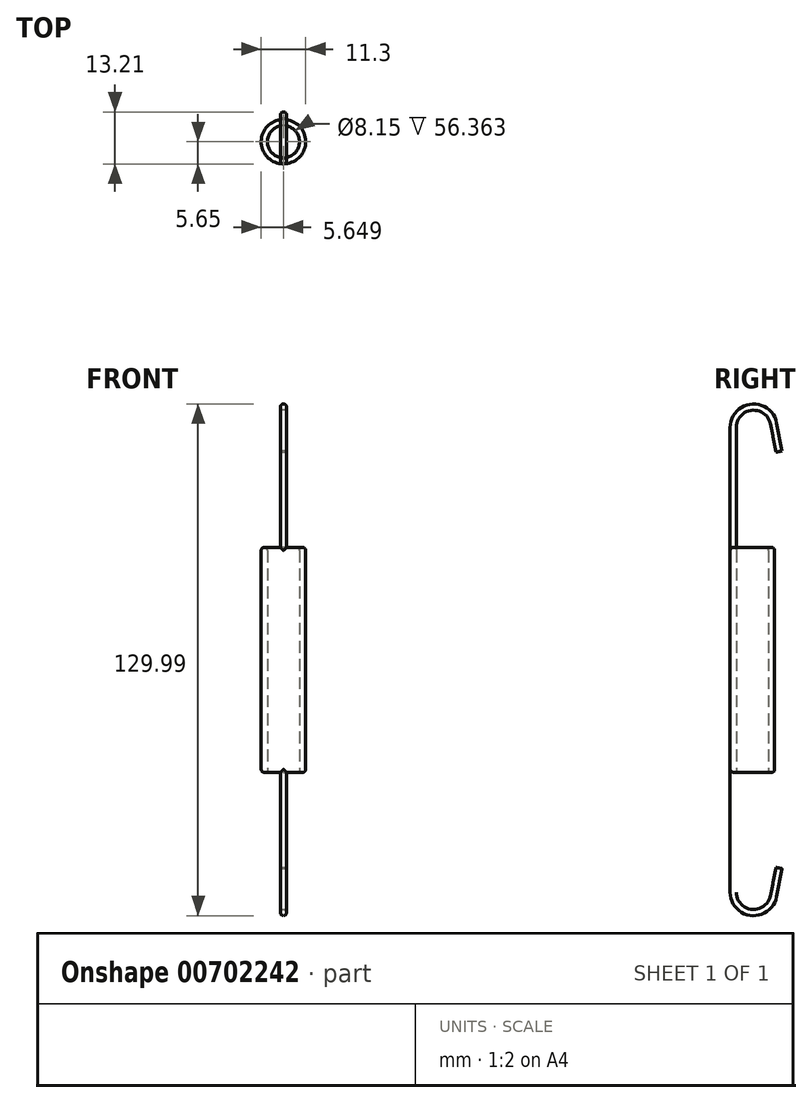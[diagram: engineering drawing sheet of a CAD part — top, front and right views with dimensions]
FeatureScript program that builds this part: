
annotation { "Feature Type Name" : "Feature", "Feature Type Description" : "" }
export const myFeature = defineFeature(function(context is Context, id is Id, definition is map)
    precondition{}
    {
        {
            var Q0;
            Q0=qCreatedBy(makeId("Top.planeOp"),FACE);
            var sketch = newSketch(context, id + "F0", { "sketchPlane" : qUnion([Q0])});
            skCircle(sketch, "E0", {"center": v(-5.65, 0) * mm, "radius": 5.65 * mm});
            skCircle(sketch, "E1", {"center": v(-5.65, 0) * mm, "radius": 4.08 * mm});
            skSolve(sketch);
        }
        {
            var Q0;
            Q0=makeQuery(id+"F0.imprint","IMPRINT",FACE,{"disambiguationData":[TD([[makeQuery(id+"F0.imprint","IMPRINT",EDGE,{"derivedFrom":sQuery(id+"F0.wireOp",EDGE,"E0")}),1.0]])]});
            extrude(context, id + "F1", {"entities" : qUnion([Q0]), "depth" : 57.15 * mm, "offsetDistance" : 25.4 * mm});
        }
        {
            var Q0;
            Q0=qCreatedBy(makeId("Right.planeOp"),FACE);
            var sketch = newSketch(context, id + "F2", { "sketchPlane" : qUnion([Q0])});
            skLineSegment(sketch, "E2.0", {"start": v(-5.65, 0) * mm, "end": v(5.65, 0) * mm});
            skLineSegment(sketch, "E3.bottom", {"start": v(-5.65, 0) * mm, "end": v(6.26, 0) * mm});
            skLineSegment(sketch, "E3.top", {"start": v(-5.65, -36.42) * mm, "end": v(6.26, -36.42) * mm});
            skLineSegment(sketch, "E3.left", {"start": v(-5.65, 0) * mm, "end": v(-5.65, -36.42) * mm});
            skLineSegment(sketch, "E3.right", {"start": v(6.26, 0) * mm, "end": v(6.26, -36.42) * mm});
            skLineSegment(sketch, "E4.0", {"start": v(-5.65, 57.15) * mm, "end": v(5.65, 57.15) * mm});
            skLineSegment(sketch, "E5.bottom", {"start": v(-5.65, 57.15) * mm, "end": v(6.26, 57.15) * mm});
            skLineSegment(sketch, "E5.top", {"start": v(-5.65, 93.57) * mm, "end": v(6.26, 93.57) * mm});
            skLineSegment(sketch, "E5.left", {"start": v(-5.65, 57.15) * mm, "end": v(-5.65, 93.57) * mm});
            skLineSegment(sketch, "E5.right", {"start": v(6.26, 57.15) * mm, "end": v(6.26, 93.57) * mm});
            skArc(sketch, "E6", {"start": v(-5.65, -30.47) * mm, "mid": v(-0.27, -36.4) * mm, "end": v(6.15, -31.62) * mm});
            skPoint(sketch, "E6.centerSnap0", {"position": v(0.3, -36.42) * mm});
            skArc(sketch, "E7", {"start": v(6.15, 88.77) * mm, "mid": v(-0.27, 93.55) * mm, "end": v(-5.65, 87.62) * mm});
            skPoint(sketch, "E7.centerSnap0", {"position": v(0.3, 93.57) * mm});
            skLineSegment(sketch, "E8", {"start": v(1.87, 81.64) * mm, "end": v(14.82, 81.64) * mm});
            skLineSegment(sketch, "E9", {"start": v(7.56, 80.48) * mm, "end": v(7.56, 83.95) * mm});
            skLineSegment(sketch, "E10", {"start": v(8.6, -24.49) * mm, "end": v(15.97, -24.49) * mm});
            skLineSegment(sketch, "E11", {"start": v(7.56, -26.21) * mm, "end": v(7.56, -20.09) * mm});
            skLineSegment(sketch, "E12", {"start": v(7.56, -24.49) * mm, "end": v(6.15, -31.62) * mm});
            skLineSegment(sketch, "E13", {"start": v(7.56, 81.64) * mm, "end": v(6.15, 88.77) * mm});
            skLineSegment(sketch, "E14.0", {"start": v(-4.08, 0) * mm, "end": v(-4.08, -30.47) * mm});
            skCircle(sketch, "E15", {"center": v(0.3, -30.47) * mm, "radius": 4.38 * mm});
            skLineSegment(sketch, "E16.0", {"start": v(6.01, -24.18) * mm, "end": v(4.6, -31.32) * mm});
            skLineSegment(sketch, "E17", {"start": v(7.56, -24.49) * mm, "end": v(6.01, -24.18) * mm});
            skLineSegment(sketch, "E18.0", {"start": v(-4.08, 57.15) * mm, "end": v(-4.08, 87.62) * mm});
            skLineSegment(sketch, "E19.0", {"start": v(6.01, 81.33) * mm, "end": v(4.6, 88.47) * mm});
            skCircle(sketch, "E20", {"center": v(0.3, 87.62) * mm, "radius": 4.38 * mm});
            skLineSegment(sketch, "E21.trimOffspring", {"start": v(-4.08, 91.65) * mm, "end": v(-4.08, 93.57) * mm});
            skLineSegment(sketch, "E22.trimOffspring", {"start": v(-4.08, -34.5) * mm, "end": v(-4.08, -36.42) * mm});
            skLineSegment(sketch, "E23", {"start": v(7.56, 81.64) * mm, "end": v(6.01, 81.33) * mm});
            skSolve(sketch);
        }
        {
            var Q0;
            {var subQ0=sQuery(id+"F2.wireOp",EDGE,"E18.0");Q0=makeQuery(id+"F2.imprint","IMPRINT",FACE,{"disambiguationData":[TD([[makeQuery(id+"F2.imprint","IMPRINT",EDGE,{"derivedFrom":subQ0}),1.0]])]});}
            var Q1;
            {var subQ0=sQuery(id+"F2.wireOp",EDGE,"E13");var subQ1=sQuery(id+"F2.wireOp",EDGE,"E5.right");var subQ2=makeQuery(id+"F2.imprint","INTERSECT",VERTEX,{"derivedFrom":[subQ1,subQ0]});Q1=makeQuery(id+"F2.imprint","IMPRINT",FACE,{"disambiguationData":[TD([[makeQuery(id+"F2.imprint","IMPRINT",EDGE,{"disambiguationData":[TD([[subQ2,1.0]])],"derivedFrom":subQ1}),-1.0]])]});}
            var Q2;
            {var subQ0=sQuery(id+"F2.wireOp",EDGE,"E23");var subQ1=sQuery(id+"F2.wireOp",EDGE,"E5.right");var subQ2=makeQuery(id+"F2.imprint","INTERSECT",VERTEX,{"derivedFrom":[subQ1,subQ0]});Q2=makeQuery(id+"F2.imprint","IMPRINT",FACE,{"disambiguationData":[TD([[makeQuery(id+"F2.imprint","IMPRINT",EDGE,{"disambiguationData":[TD([[subQ2,-1.0]])],"derivedFrom":subQ1}),-1.0]])]});}
            var Q3;
            {var subQ0=sQuery(id+"F2.wireOp",EDGE,"E23");var subQ1=sQuery(id+"F2.wireOp",EDGE,"E5.right");var subQ2=makeQuery(id+"F2.imprint","INTERSECT",VERTEX,{"derivedFrom":[subQ1,subQ0]});Q3=makeQuery(id+"F2.imprint","IMPRINT",FACE,{"disambiguationData":[TD([[makeQuery(id+"F2.imprint","IMPRINT",EDGE,{"disambiguationData":[TD([[subQ2,-1.0]])],"derivedFrom":subQ1}),1.0]])]});}
            var Q4;
            {var subQ9=sQuery(id+"F2.wireOp",EDGE,"E14.0");Q4=makeQuery(id+"F2.imprint","IMPRINT",FACE,{"disambiguationData":[TD([[makeQuery(id+"F2.imprint","IMPRINT",EDGE,{"derivedFrom":subQ9}),-1.0]])]});}
            var Q5;
            {var subQ0=sQuery(id+"F2.wireOp",EDGE,"E17");var subQ1=sQuery(id+"F2.wireOp",EDGE,"E3.right");var subQ2=makeQuery(id+"F2.imprint","INTERSECT",VERTEX,{"derivedFrom":[subQ1,subQ0]});Q5=makeQuery(id+"F2.imprint","IMPRINT",FACE,{"disambiguationData":[TD([[makeQuery(id+"F2.imprint","IMPRINT",EDGE,{"disambiguationData":[TD([[subQ2,-1.0]])],"derivedFrom":subQ1}),1.0]])]});}
            extrude(context, id + "F3", {"entities" : qUnion([Q0, Q1, Q2, Q3, Q4, Q5]), "operationType" : NewBodyOperationType.ADD, "oppositeDirection" : true, "depth" : 11.3 * mm, "offsetDistance" : 25.4 * mm});
        }
        {
            var Q0;
            Q0=makeQuery(id+"F1.opExtrude","CAP_FACE",FACE,{"disambiguationData":[OSD([sQuery(id+"F0.wireOp",EDGE,"E0"),sQuery(id+"F0.wireOp",EDGE,"E1")])],"isStart":false});
            var sketch = newSketch(context, id + "F4", { "sketchPlane" : qUnion([Q0])});
            skLineSegment(sketch, "E24", {"start": v(-5.65, 0) * mm, "end": v(-5.65, -4.08) * mm});
            skLineSegment(sketch, "E25", {"start": v(-5.65, -4.08) * mm, "end": v(-6.44, -4.08) * mm});
            skLineSegment(sketch, "E26", {"start": v(-6.44, -4.08) * mm, "end": v(-4.86, -4.08) * mm});
            skLineSegment(sketch, "E27.bottom", {"start": v(-6.44, -4.08) * mm, "end": v(-11.86, -4.08) * mm});
            skLineSegment(sketch, "E27.top", {"start": v(-6.44, -7.3) * mm, "end": v(-11.86, -7.3) * mm});
            skLineSegment(sketch, "E27.left", {"start": v(-6.44, -4.08) * mm, "end": v(-6.44, -7.3) * mm});
            skLineSegment(sketch, "E27.right", {"start": v(-11.86, -4.08) * mm, "end": v(-11.86, -7.3) * mm});
            skLineSegment(sketch, "E28.bottom", {"start": v(-4.86, -4.08) * mm, "end": v(1.36, -4.08) * mm});
            skLineSegment(sketch, "E28.top", {"start": v(-4.86, -7.3) * mm, "end": v(1.36, -7.3) * mm});
            skLineSegment(sketch, "E28.left", {"start": v(-4.86, -4.08) * mm, "end": v(-4.86, -7.3) * mm});
            skLineSegment(sketch, "E28.right", {"start": v(1.36, -4.08) * mm, "end": v(1.36, -7.3) * mm});
            skLineSegment(sketch, "E29.bottom", {"start": v(-11.86, -4.08) * mm, "end": v(-6.44, -4.08) * mm});
            skLineSegment(sketch, "E29.top", {"start": v(-11.86, 8.59) * mm, "end": v(-6.44, 8.59) * mm});
            skLineSegment(sketch, "E29.left", {"start": v(-11.86, -4.08) * mm, "end": v(-11.86, 8.59) * mm});
            skLineSegment(sketch, "E29.right", {"start": v(-6.44, -4.08) * mm, "end": v(-6.44, 8.59) * mm});
            skLineSegment(sketch, "E30.top", {"start": v(-4.86, 8.63) * mm, "end": v(1.36, 8.63) * mm});
            skLineSegment(sketch, "E30.left", {"start": v(-4.86, -4.08) * mm, "end": v(-4.86, 8.63) * mm});
            skLineSegment(sketch, "E30.right", {"start": v(1.36, -4.08) * mm, "end": v(1.36, 8.63) * mm});
            skSolve(sketch);
        }
        {
            var Q0;
            {var subQ2=sQuery(id+"F4.wireOp",EDGE,"E29.top");Q0=makeQuery(id+"F4.imprint","IMPRINT",FACE,{"disambiguationData":[TD([[makeQuery(id+"F4.imprint","IMPRINT",EDGE,{"derivedFrom":subQ2}),-1.0]])]});}
            var Q1;
            {var subQ2=sQuery(id+"F0.wireOp",EDGE,"E1");var subQ5=sQuery(id+"F4.wireOp",EDGE,"E29.right");var subQ7=makeQuery(id+"F1.opExtrude","CAP_EDGE",EDGE,{"disambiguationData":[OSD([subQ2])],"isStart":false});var subQ10=makeQuery(id+"F4.imprint","INTERSECT",VERTEX,{"disambiguationData":[OD(0.0)],"derivedFrom":[subQ7,subQ5]});Q1=makeQuery(id+"F4.imprint","IMPRINT",FACE,{"disambiguationData":[TD([[makeQuery(id+"F4.imprint","IMPRINT",EDGE,{"disambiguationData":[TD([[subQ10,1.0]])],"derivedFrom":subQ7}),-1.0]])]});}
            var Q2;
            {var subQ0=sQuery(id+"F4.wireOp",EDGE,"E29.right");var subQ1=makeQuery(id+"F1.opExtrude","CAP_EDGE",EDGE,{"disambiguationData":[OSD([sQuery(id+"F0.wireOp",EDGE,"E1")])],"isStart":false});var subQ2=makeQuery(id+"F4.imprint","INTERSECT",VERTEX,{"disambiguationData":[OD(0.0)],"derivedFrom":[subQ1,subQ0]});Q2=makeQuery(id+"F4.imprint","IMPRINT",FACE,{"disambiguationData":[TD([[makeQuery(id+"F4.imprint","IMPRINT",EDGE,{"disambiguationData":[TD([[subQ2,-1.0]])],"derivedFrom":subQ0}),1.0]])]});}
            var Q3;
            Q3=makeQuery(id+"F4.imprint","IMPRINT",FACE,{"disambiguationData":[TD([[makeQuery(id+"F4.imprint","IMPRINT",EDGE,{"derivedFrom":sQuery(id+"F4.wireOp",EDGE,"E27.top")}),-1.0]])]});
            var Q4;
            {var subQ1=sQuery(id+"F4.wireOp",EDGE,"E30.top");Q4=makeQuery(id+"F4.imprint","IMPRINT",FACE,{"disambiguationData":[TD([[makeQuery(id+"F4.imprint","IMPRINT",EDGE,{"derivedFrom":subQ1}),-1.0]])]});}
            var Q5;
            {var subQ0=sQuery(id+"F4.wireOp",EDGE,"E30.left");var subQ2=sQuery(id+"F0.wireOp",EDGE,"E1");var subQ5=makeQuery(id+"F1.opExtrude","CAP_EDGE",EDGE,{"disambiguationData":[OSD([subQ2])],"isStart":false});var subQ10=makeQuery(id+"F4.imprint","INTERSECT",VERTEX,{"disambiguationData":[OD(0.0)],"derivedFrom":[subQ5,subQ0]});Q5=makeQuery(id+"F4.imprint","IMPRINT",FACE,{"disambiguationData":[TD([[makeQuery(id+"F4.imprint","IMPRINT",EDGE,{"disambiguationData":[TD([[subQ10,-1.0]])],"derivedFrom":subQ5}),-1.0]])]});}
            var Q6;
            {var subQ0=sQuery(id+"F4.wireOp",EDGE,"E30.left");var subQ1=makeQuery(id+"F1.opExtrude","CAP_EDGE",EDGE,{"disambiguationData":[OSD([sQuery(id+"F0.wireOp",EDGE,"E1")])],"isStart":false});var subQ2=makeQuery(id+"F4.imprint","INTERSECT",VERTEX,{"disambiguationData":[OD(0.0)],"derivedFrom":[subQ1,subQ0]});Q6=makeQuery(id+"F4.imprint","IMPRINT",FACE,{"disambiguationData":[TD([[makeQuery(id+"F4.imprint","IMPRINT",EDGE,{"disambiguationData":[TD([[subQ2,-1.0]])],"derivedFrom":subQ0}),-1.0]])]});}
            var Q7;
            Q7=makeQuery(id+"F4.imprint","IMPRINT",FACE,{"disambiguationData":[TD([[makeQuery(id+"F4.imprint","IMPRINT",EDGE,{"derivedFrom":sQuery(id+"F4.wireOp",EDGE,"E28.top")}),1.0]])]});
            extrude(context, id + "F5", {"entities" : qUnion([Q0, Q1, Q2, Q3, Q4, Q5, Q6, Q7]), "operationType" : NewBodyOperationType.REMOVE, "depth" : 76.2 * mm, "offsetDistance" : 25.4 * mm});
        }
        {
            var Q0;
            Q0=makeQuery(id+"F1.opExtrude","CAP_FACE",FACE,{"disambiguationData":[OSD([sQuery(id+"F0.wireOp",EDGE,"E0"),sQuery(id+"F0.wireOp",EDGE,"E1")])],"isStart":true});
            var sketch = newSketch(context, id + "F6", { "sketchPlane" : qUnion([Q0])});
            skLineSegment(sketch, "E31", {"start": v(-5.65, 0) * mm, "end": v(-5.65, 4.08) * mm});
            skLineSegment(sketch, "E32", {"start": v(-5.65, 4.08) * mm, "end": v(-6.44, 4.08) * mm});
            skLineSegment(sketch, "E33", {"start": v(-6.44, 4.08) * mm, "end": v(-4.86, 4.08) * mm});
            skLineSegment(sketch, "E34.bottom", {"start": v(-6.44, 4.08) * mm, "end": v(-12.15, 4.08) * mm});
            skLineSegment(sketch, "E34.top", {"start": v(-6.44, 8.66) * mm, "end": v(-12.15, 8.66) * mm});
            skLineSegment(sketch, "E34.left", {"start": v(-6.44, 4.08) * mm, "end": v(-6.44, 8.66) * mm});
            skLineSegment(sketch, "E34.right", {"start": v(-12.15, 4.08) * mm, "end": v(-12.15, 8.66) * mm});
            skLineSegment(sketch, "E35.bottom", {"start": v(-4.86, 4.08) * mm, "end": v(3.43, 4.08) * mm});
            skLineSegment(sketch, "E35.top", {"start": v(-4.86, 8.66) * mm, "end": v(3.43, 8.66) * mm});
            skLineSegment(sketch, "E35.left", {"start": v(-4.86, 4.08) * mm, "end": v(-4.86, 8.66) * mm});
            skLineSegment(sketch, "E35.right", {"start": v(3.43, 4.08) * mm, "end": v(3.43, 8.66) * mm});
            skLineSegment(sketch, "E36.bottom", {"start": v(-12.15, 4.08) * mm, "end": v(-6.44, 4.08) * mm});
            skLineSegment(sketch, "E36.top", {"start": v(-12.15, -7.97) * mm, "end": v(-6.44, -7.97) * mm});
            skLineSegment(sketch, "E36.left", {"start": v(-12.15, 4.08) * mm, "end": v(-12.15, -7.97) * mm});
            skLineSegment(sketch, "E36.right", {"start": v(-6.44, 4.08) * mm, "end": v(-6.44, -7.97) * mm});
            skLineSegment(sketch, "E37.top", {"start": v(-4.86, -7.97) * mm, "end": v(3.43, -7.97) * mm});
            skLineSegment(sketch, "E37.left", {"start": v(-4.86, 4.08) * mm, "end": v(-4.86, -7.97) * mm});
            skLineSegment(sketch, "E37.right", {"start": v(3.43, 4.08) * mm, "end": v(3.43, -7.97) * mm});
            skSolve(sketch);
        }
        {
            var Q0;
            {var subQ1=sQuery(id+"F6.wireOp",EDGE,"E37.top");Q0=makeQuery(id+"F6.imprint","IMPRINT",FACE,{"disambiguationData":[TD([[makeQuery(id+"F6.imprint","IMPRINT",EDGE,{"derivedFrom":subQ1}),1.0]])]});}
            var Q1;
            Q1=makeQuery(id+"F6.imprint","IMPRINT",FACE,{"disambiguationData":[TD([[makeQuery(id+"F6.imprint","IMPRINT",EDGE,{"derivedFrom":sQuery(id+"F6.wireOp",EDGE,"E35.top")}),-1.0]])]});
            var Q2;
            {var subQ0=sQuery(id+"F6.wireOp",EDGE,"E37.left");var subQ2=sQuery(id+"F0.wireOp",EDGE,"E1");var subQ5=makeQuery(id+"F1.opExtrude","CAP_EDGE",EDGE,{"disambiguationData":[OSD([subQ2])],"isStart":true});var subQ10=makeQuery(id+"F6.imprint","INTERSECT",VERTEX,{"disambiguationData":[OD(0.0)],"derivedFrom":[subQ5,subQ0]});Q2=makeQuery(id+"F6.imprint","IMPRINT",FACE,{"disambiguationData":[TD([[makeQuery(id+"F6.imprint","IMPRINT",EDGE,{"disambiguationData":[TD([[subQ10,-1.0]])],"derivedFrom":subQ5}),1.0]])]});}
            var Q3;
            {var subQ0=sQuery(id+"F6.wireOp",EDGE,"E37.left");var subQ1=makeQuery(id+"F1.opExtrude","CAP_EDGE",EDGE,{"disambiguationData":[OSD([sQuery(id+"F0.wireOp",EDGE,"E1")])],"isStart":true});var subQ2=makeQuery(id+"F6.imprint","INTERSECT",VERTEX,{"disambiguationData":[OD(0.0)],"derivedFrom":[subQ1,subQ0]});Q3=makeQuery(id+"F6.imprint","IMPRINT",FACE,{"disambiguationData":[TD([[makeQuery(id+"F6.imprint","IMPRINT",EDGE,{"disambiguationData":[TD([[subQ2,-1.0]])],"derivedFrom":subQ0}),1.0]])]});}
            var Q4;
            {var subQ2=sQuery(id+"F6.wireOp",EDGE,"E36.top");Q4=makeQuery(id+"F6.imprint","IMPRINT",FACE,{"disambiguationData":[TD([[makeQuery(id+"F6.imprint","IMPRINT",EDGE,{"derivedFrom":subQ2}),1.0]])]});}
            var Q5;
            {var subQ2=sQuery(id+"F0.wireOp",EDGE,"E1");var subQ5=sQuery(id+"F6.wireOp",EDGE,"E36.right");var subQ7=makeQuery(id+"F1.opExtrude","CAP_EDGE",EDGE,{"disambiguationData":[OSD([subQ2])],"isStart":true});var subQ10=makeQuery(id+"F6.imprint","INTERSECT",VERTEX,{"disambiguationData":[OD(0.0)],"derivedFrom":[subQ7,subQ5]});Q5=makeQuery(id+"F6.imprint","IMPRINT",FACE,{"disambiguationData":[TD([[makeQuery(id+"F6.imprint","IMPRINT",EDGE,{"disambiguationData":[TD([[subQ10,1.0]])],"derivedFrom":subQ7}),1.0]])]});}
            var Q6;
            {var subQ0=sQuery(id+"F6.wireOp",EDGE,"E36.right");var subQ1=makeQuery(id+"F1.opExtrude","CAP_EDGE",EDGE,{"disambiguationData":[OSD([sQuery(id+"F0.wireOp",EDGE,"E1")])],"isStart":true});var subQ2=makeQuery(id+"F6.imprint","INTERSECT",VERTEX,{"disambiguationData":[OD(0.0)],"derivedFrom":[subQ1,subQ0]});Q6=makeQuery(id+"F6.imprint","IMPRINT",FACE,{"disambiguationData":[TD([[makeQuery(id+"F6.imprint","IMPRINT",EDGE,{"disambiguationData":[TD([[subQ2,-1.0]])],"derivedFrom":subQ0}),-1.0]])]});}
            var Q7;
            Q7=makeQuery(id+"F6.imprint","IMPRINT",FACE,{"disambiguationData":[TD([[makeQuery(id+"F6.imprint","IMPRINT",EDGE,{"derivedFrom":sQuery(id+"F6.wireOp",EDGE,"E34.top")}),1.0]])]});
            extrude(context, id + "F7", {"entities" : qUnion([Q0, Q1, Q2, Q3, Q4, Q5, Q6, Q7]), "operationType" : NewBodyOperationType.REMOVE, "depth" : 76.2 * mm, "offsetDistance" : 25.4 * mm});
        }
        {
            var Q0;
            Q0=makeQuery(id+"F7.boolean.opBoolean","INTERSECT",EDGE,{"derivedFrom":[makeQuery(id+"F3.opExtrude","SWEPT_FACE",FACE,{"disambiguationData":[OSD([sQuery(id+"F2.wireOp",EDGE,"E3.left")])]}),makeQuery(id+"F7.opExtrude","SWEPT_FACE",FACE,{"disambiguationData":[OSD([sQuery(id+"F6.wireOp",EDGE,"E35.left"),sQuery(id+"F6.wireOp",EDGE,"E37.left")])]})]});
            var Q1;
            Q1=makeQuery(id+"F7.boolean.opBoolean","INTERSECT",EDGE,{"derivedFrom":[makeQuery(id+"F3.opExtrude","SWEPT_FACE",FACE,{"disambiguationData":[OSD([sQuery(id+"F2.wireOp",EDGE,"E3.left")])]}),makeQuery(id+"F7.opExtrude","SWEPT_FACE",FACE,{"disambiguationData":[OSD([sQuery(id+"F6.wireOp",EDGE,"E34.left"),sQuery(id+"F6.wireOp",EDGE,"E36.right")])]})]});
            var Q2;
            Q2=makeQuery(id+"F7.boolean.opBoolean","INTERSECT",EDGE,{"derivedFrom":[makeQuery(id+"F3.opExtrude","SWEPT_FACE",FACE,{"disambiguationData":[OSD([sQuery(id+"F2.wireOp",EDGE,"E14.0")])]}),makeQuery(id+"F7.opExtrude","SWEPT_FACE",FACE,{"disambiguationData":[OSD([sQuery(id+"F6.wireOp",EDGE,"E35.left"),sQuery(id+"F6.wireOp",EDGE,"E37.left")])]})]});
            var Q3;
            Q3=makeQuery(id+"F7.boolean.opBoolean","INTERSECT",EDGE,{"derivedFrom":[makeQuery(id+"F3.opExtrude","SWEPT_FACE",FACE,{"disambiguationData":[OSD([sQuery(id+"F2.wireOp",EDGE,"E14.0")])]}),makeQuery(id+"F7.opExtrude","SWEPT_FACE",FACE,{"disambiguationData":[OSD([sQuery(id+"F6.wireOp",EDGE,"E34.left"),sQuery(id+"F6.wireOp",EDGE,"E36.right")])]})]});
            var Q4;
            Q4=makeQuery(id+"F5.boolean.opBoolean","INTERSECT",EDGE,{"derivedFrom":[makeQuery(id+"F3.opExtrude","SWEPT_FACE",FACE,{"disambiguationData":[OSD([sQuery(id+"F2.wireOp",EDGE,"E18.0")])]}),makeQuery(id+"F5.opExtrude","SWEPT_FACE",FACE,{"disambiguationData":[OSD([sQuery(id+"F4.wireOp",EDGE,"E27.left"),sQuery(id+"F4.wireOp",EDGE,"E29.right")])]})]});
            var Q5;
            Q5=makeQuery(id+"F5.boolean.opBoolean","INTERSECT",EDGE,{"derivedFrom":[makeQuery(id+"F3.opExtrude","SWEPT_FACE",FACE,{"disambiguationData":[OSD([sQuery(id+"F2.wireOp",EDGE,"E5.left")])]}),makeQuery(id+"F5.opExtrude","SWEPT_FACE",FACE,{"disambiguationData":[OSD([sQuery(id+"F4.wireOp",EDGE,"E27.left"),sQuery(id+"F4.wireOp",EDGE,"E29.right")])]})]});
            var Q6;
            Q6=makeQuery(id+"F5.boolean.opBoolean","INTERSECT",EDGE,{"derivedFrom":[makeQuery(id+"F3.opExtrude","SWEPT_FACE",FACE,{"disambiguationData":[OSD([sQuery(id+"F2.wireOp",EDGE,"E5.left")])]}),makeQuery(id+"F5.opExtrude","SWEPT_FACE",FACE,{"disambiguationData":[OSD([sQuery(id+"F4.wireOp",EDGE,"E28.left"),sQuery(id+"F4.wireOp",EDGE,"E30.left")])]})]});
            var Q7;
            Q7=makeQuery(id+"F5.boolean.opBoolean","INTERSECT",EDGE,{"derivedFrom":[makeQuery(id+"F3.opExtrude","SWEPT_FACE",FACE,{"disambiguationData":[OSD([sQuery(id+"F2.wireOp",EDGE,"E18.0")])]}),makeQuery(id+"F5.opExtrude","SWEPT_FACE",FACE,{"disambiguationData":[OSD([sQuery(id+"F4.wireOp",EDGE,"E28.left"),sQuery(id+"F4.wireOp",EDGE,"E30.left")])]})]});
            fillet(context, id + "F8", {"entities" : qUnion([Q0, Q1, Q2, Q3, Q4, Q5, Q6, Q7]), "radius" : 0.79 * mm, "tangentPropagation" : true, "allowEdgeOverflow" : false});
        }
        {
            var Q0;
            {var subQ0=sQuery(id+"F0.wireOp",EDGE,"E0");var subQ1=makeQuery(id+"F1.opExtrude","SWEPT_FACE",FACE,{"disambiguationData":[OSD([subQ0])]});var subQ2=makeQuery(id+"F3.opExtrude","SWEPT_FACE",FACE,{"disambiguationData":[OSD([sQuery(id+"F2.wireOp",EDGE,"E5.bottom")])]});var subQ3=makeQuery(id+"F1.opExtrude","CAP_EDGE",EDGE,{"disambiguationData":[OSD([subQ0])],"isStart":false});var subQ4=makeQuery(id+"F3.boolean.opBoolean","SPLIT",EDGE,{"disambiguationData":[topologyDisambiguationEdgeConnected([subQ1,subQ2]),OD(1.0)],"derivedFrom":subQ3});var subQ5=makeQuery(id+"F3.boolean.opBoolean","SPLIT",EDGE,{"disambiguationData":[topologyDisambiguationEdgeConnected([subQ1,subQ2]),OD(0.0)],"derivedFrom":subQ3});Q0=makeQuery(id+"F8.opFillet","MERGE",EDGE,{"derivedFrom":[makeQuery(id+"F5.boolean.opBoolean","MERGE",EDGE,{"derivedFrom":[makeQuery(id+"F3.boolean.opBoolean","SPLIT",EDGE,{"disambiguationData":[topologyDisambiguationEdgeConnected([subQ1,makeQuery(id+"F1.opExtrude","CAP_FACE",FACE,{"disambiguationData":[OSD([subQ0,sQuery(id+"F0.wireOp",EDGE,"E1")])],"isStart":false})])],"derivedFrom":subQ3}),subQ5,subQ4]}),makeQuery(id+"F5.boolean.opBoolean","SPLIT",EDGE,{"derivedFrom":subQ5}),makeQuery(id+"F5.boolean.opBoolean","SPLIT",EDGE,{"derivedFrom":subQ4})]});}
            var Q1;
            Q1=makeQuery(id+"F5.boolean.opBoolean","INTERSECT",EDGE,{"derivedFrom":[makeQuery(id+"F5.opExtrude","CAP_FACE",FACE,{"disambiguationData":[OSD([sQuery(id+"F4.wireOp",EDGE,"E27.top"),sQuery(id+"F4.wireOp",EDGE,"E27.left"),sQuery(id+"F4.wireOp",EDGE,"E27.right"),sQuery(id+"F4.wireOp",EDGE,"E29.top"),sQuery(id+"F4.wireOp",EDGE,"E29.left"),sQuery(id+"F4.wireOp",EDGE,"E29.right")])],"isStart":true}),makeQuery(id+"F5.opExtrude","CAP_FACE",FACE,{"disambiguationData":[OSD([sQuery(id+"F4.wireOp",EDGE,"E28.top"),sQuery(id+"F4.wireOp",EDGE,"E28.left"),sQuery(id+"F4.wireOp",EDGE,"E28.right"),sQuery(id+"F4.wireOp",EDGE,"E30.top"),sQuery(id+"F4.wireOp",EDGE,"E30.left"),sQuery(id+"F4.wireOp",EDGE,"E30.right")])],"isStart":true})]});
            fillet(context, id + "F9", {"entities" : qUnion([Q0, Q1]), "radius" : 0.79 * mm, "tangentPropagation" : true, "allowEdgeOverflow" : false});
        }
        {
            var Q0;
            {var subQ0=sQuery(id+"F0.wireOp",EDGE,"E0");var subQ1=makeQuery(id+"F1.opExtrude","SWEPT_FACE",FACE,{"disambiguationData":[OSD([subQ0])]});var subQ2=makeQuery(id+"F3.opExtrude","SWEPT_FACE",FACE,{"disambiguationData":[OSD([sQuery(id+"F2.wireOp",EDGE,"E3.bottom")])]});var subQ3=makeQuery(id+"F1.opExtrude","CAP_EDGE",EDGE,{"disambiguationData":[OSD([subQ0])],"isStart":true});var subQ4=makeQuery(id+"F3.boolean.opBoolean","SPLIT",EDGE,{"disambiguationData":[topologyDisambiguationEdgeConnected([subQ1,subQ2]),OD(1.0)],"derivedFrom":subQ3});var subQ5=makeQuery(id+"F3.boolean.opBoolean","SPLIT",EDGE,{"disambiguationData":[topologyDisambiguationEdgeConnected([subQ1,subQ2]),OD(0.0)],"derivedFrom":subQ3});Q0=makeQuery(id+"F8.opFillet","MERGE",EDGE,{"derivedFrom":[makeQuery(id+"F7.boolean.opBoolean","MERGE",EDGE,{"derivedFrom":[makeQuery(id+"F3.boolean.opBoolean","SPLIT",EDGE,{"disambiguationData":[topologyDisambiguationEdgeConnected([subQ1,makeQuery(id+"F1.opExtrude","CAP_FACE",FACE,{"disambiguationData":[OSD([subQ0,sQuery(id+"F0.wireOp",EDGE,"E1")])],"isStart":true})])],"derivedFrom":subQ3}),subQ5,subQ4]}),makeQuery(id+"F7.boolean.opBoolean","SPLIT",EDGE,{"derivedFrom":subQ5}),makeQuery(id+"F7.boolean.opBoolean","SPLIT",EDGE,{"derivedFrom":subQ4})]});}
            fillet(context, id + "F10", {"entities" : qUnion([Q0]), "radius" : 0.79 * mm, "tangentPropagation" : true, "allowEdgeOverflow" : false});
        }
    });
